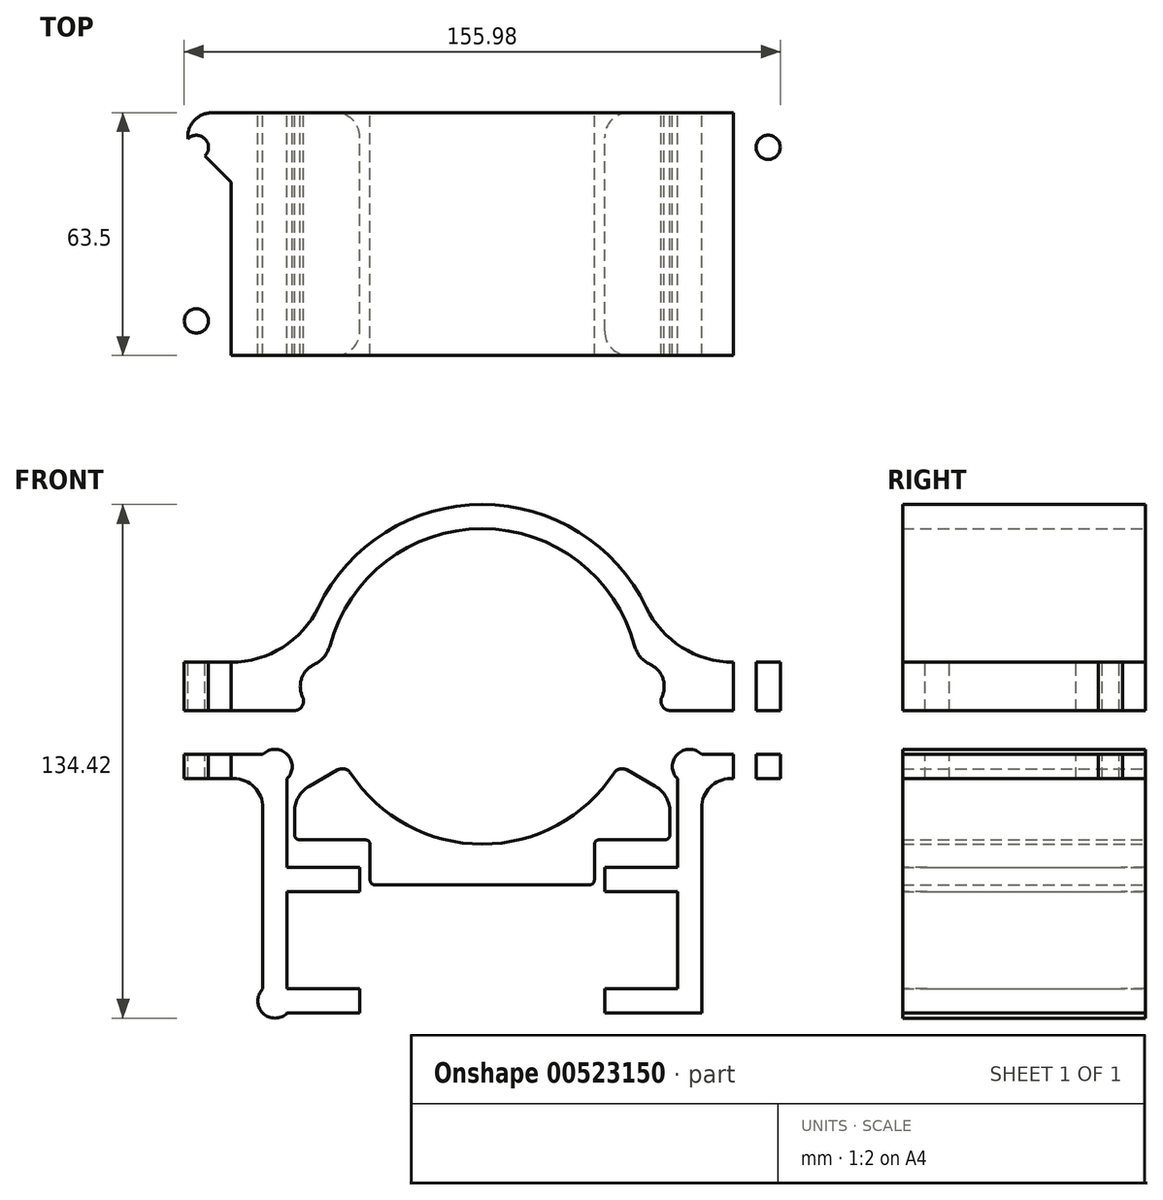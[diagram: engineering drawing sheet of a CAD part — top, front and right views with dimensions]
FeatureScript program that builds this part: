
annotation { "Feature Type Name" : "Feature", "Feature Type Description" : "" }
export const myFeature = defineFeature(function(context is Context, id is Id, definition is map)
    precondition{}
    {
        {
            var Q0;
            Q0=qCreatedBy(makeId("Front.planeOp"),FACE);
            var sketch = newSketch(context, id + "F0", { "sketchPlane" : qUnion([Q0])});
            skArc(sketch, "E0", {"start": v(-40.79, -6.33) * mm, "mid": v(-40.79, -6.34) * mm, "end": v(-40.78, -6.35) * mm});
            skArc(sketch, "E1", {"start": v(-43.98, 5.74) * mm, "mid": v(-47.25, 2.14) * mm, "end": v(-47.01, -2.72) * mm});
            skArc(sketch, "E2", {"start": v(47.01, -2.72) * mm, "mid": v(47.25, 2.14) * mm, "end": v(43.98, 5.74) * mm});
            skArc(sketch, "E3.trimOffspring", {"start": v(39.87, 10.67) * mm, "mid": v(0, 41.28) * mm, "end": v(-39.87, 10.67) * mm});
            skLineSegment(sketch, "E4.bottom", {"start": v(-83.86, 6.35) * mm, "end": v(-65.76, 6.35) * mm});
            skLineSegment(sketch, "E4.top", {"start": v(-83.86, -6.35) * mm, "end": v(-49.3, -6.35) * mm});
            skLineSegment(sketch, "E4.left", {"start": v(-83.86, 6.35) * mm, "end": v(-83.86, -6.35) * mm});
            skLineSegment(sketch, "E4.right", {"start": v(83.86, 6.35) * mm, "end": v(83.86, -6.35) * mm});
            skLineSegment(sketch, "E5.trimOffspring", {"start": v(-41.28, 6.35) * mm, "end": v(-40.78, 6.35) * mm});
            skLineSegment(sketch, "E6.trimOffspring", {"start": v(40.78, 6.35) * mm, "end": v(41.28, 6.35) * mm});
            skLineSegment(sketch, "E7.trimOffspring", {"start": v(49.3, -6.35) * mm, "end": v(83.86, -6.35) * mm});
            skLineSegment(sketch, "E8", {"start": v(-37.88, -21.87) * mm, "end": v(-41.24, -23.81) * mm});
            skLineSegment(sketch, "E9.MirrorCS", {"start": v(37.88, -21.87) * mm, "end": v(41.24, -23.81) * mm});
            skPoint(sketch, "E10.orphan", {"position": v(-49.1, -28.35) * mm});
            skPoint(sketch, "E11.orphan", {"position": v(49.1, -28.35) * mm});
            skArc(sketch, "E12.trimOffspring", {"start": v(40.78, -6.35) * mm, "mid": v(40.79, -6.34) * mm, "end": v(40.79, -6.33) * mm});
            skArc(sketch, "E13.trimOffspring", {"start": v(-34.49, -22.67) * mm, "mid": v(0, -41.28) * mm, "end": v(34.49, -22.67) * mm});
            skLineSegment(sketch, "E14.trimOffspring", {"start": v(65.76, 6.35) * mm, "end": v(83.86, 6.35) * mm});
            skArc(sketch, "E15.trimOffspring", {"start": v(42.89, 20.7) * mm, "mid": v(0, 47.62) * mm, "end": v(-42.89, 20.7) * mm});
            skArc(sketch, "E16.filletArc", {"start": v(-49.3, -6.35) * mm, "mid": v(-47.16, -5.17) * mm, "end": v(-47.01, -2.72) * mm});
            skArc(sketch, "E17.filletArc", {"start": v(47.01, -2.72) * mm, "mid": v(47.16, -5.17) * mm, "end": v(49.3, -6.35) * mm});
            skPoint(sketch, "E18.visualSharp", {"position": v(-47.2, 6.35) * mm});
            skArc(sketch, "E18.filletArc", {"start": v(-65.76, 6.35) * mm, "mid": v(-52.26, 10.24) * mm, "end": v(-42.89, 20.7) * mm});
            skPoint(sketch, "E19.visualSharp", {"position": v(47.2, 6.35) * mm});
            skArc(sketch, "E19.filletArc", {"start": v(42.89, 20.7) * mm, "mid": v(52.26, 10.24) * mm, "end": v(65.76, 6.35) * mm});
            skLineSegment(sketch, "E20", {"start": v(-41.24, -23.81) * mm, "end": v(-45.29, -26.15) * mm});
            skLineSegment(sketch, "E21", {"start": v(-29.34, -51.94) * mm, "end": v(29.34, -51.94) * mm});
            skLineSegment(sketch, "E22", {"start": v(45.29, -26.15) * mm, "end": v(41.24, -23.81) * mm});
            skPoint(sketch, "E23.visualSharp", {"position": v(-40.79, 6.33) * mm});
            skArc(sketch, "E23.filletArc", {"start": v(-43.98, 5.74) * mm, "mid": v(-41.39, 7.75) * mm, "end": v(-39.87, 10.67) * mm});
            skPoint(sketch, "E24.visualSharp", {"position": v(40.79, 6.33) * mm});
            skArc(sketch, "E24.filletArc", {"start": v(39.87, 10.67) * mm, "mid": v(41.39, 7.75) * mm, "end": v(43.98, 5.74) * mm});
            skLineSegment(sketch, "E25", {"start": v(-49.1, -32.75) * mm, "end": v(-49.1, -40.14) * mm});
            skLineSegment(sketch, "E26", {"start": v(49.1, -32.75) * mm, "end": v(49.1, -40.14) * mm});
            skPoint(sketch, "E27.visualSharp", {"position": v(-35.75, -20.64) * mm});
            skArc(sketch, "E27.filletArc", {"start": v(-34.49, -22.67) * mm, "mid": v(-36.03, -21.6) * mm, "end": v(-37.88, -21.87) * mm});
            skPoint(sketch, "E28.visualSharp", {"position": v(35.75, -20.64) * mm});
            skArc(sketch, "E28.filletArc", {"start": v(37.88, -21.87) * mm, "mid": v(36.03, -21.6) * mm, "end": v(34.49, -22.67) * mm});
            skArc(sketch, "E29.filletArc", {"start": v(-45.29, -26.15) * mm, "mid": v(-48.08, -28.94) * mm, "end": v(-49.1, -32.75) * mm});
            skArc(sketch, "E30.filletArc", {"start": v(49.1, -32.75) * mm, "mid": v(48.08, -28.94) * mm, "end": v(45.29, -26.15) * mm});
            skLineSegment(sketch, "E31.bottom", {"start": v(-51.07, -53.74) * mm, "end": v(-32.02, -53.74) * mm});
            skLineSegment(sketch, "E31.top", {"start": v(-51.07, -79.14) * mm, "end": v(-32.02, -79.14) * mm});
            skLineSegment(sketch, "E31.left", {"start": v(-51.07, -53.74) * mm, "end": v(-51.07, -79.14) * mm});
            skLineSegment(sketch, "E31.right", {"start": v(51.07, -53.74) * mm, "end": v(51.07, -79.14) * mm});
            skPoint(sketch, "E31.middle", {"position": v(0, -66.44) * mm});
            skLineSegment(sketch, "E32.0", {"start": v(-51.07, -85.49) * mm, "end": v(-32.02, -85.49) * mm});
            skLineSegment(sketch, "E32.1", {"start": v(-57.42, -47.39) * mm, "end": v(-57.42, -79.14) * mm});
            skLineSegment(sketch, "E32.2", {"start": v(-51.07, -47.39) * mm, "end": v(-32.02, -47.39) * mm});
            skLineSegment(sketch, "E32.3", {"start": v(57.42, -47.39) * mm, "end": v(57.42, -85.49) * mm});
            skLineSegment(sketch, "E33", {"start": v(-32.02, -47.39) * mm, "end": v(-32.02, -53.74) * mm});
            skLineSegment(sketch, "E34.MirrorCS", {"start": v(32.02, -47.39) * mm, "end": v(32.02, -53.74) * mm});
            skLineSegment(sketch, "E35.trimOffspring", {"start": v(32.02, -53.74) * mm, "end": v(51.07, -53.74) * mm});
            skLineSegment(sketch, "E36.trimOffspring", {"start": v(32.02, -47.39) * mm, "end": v(51.07, -47.39) * mm});
            skLineSegment(sketch, "E37.trimOffspring", {"start": v(32.02, -79.14) * mm, "end": v(32.02, -85.49) * mm});
            skLineSegment(sketch, "E38.trimOffspring", {"start": v(-32.02, -79.14) * mm, "end": v(-32.02, -85.49) * mm});
            skLineSegment(sketch, "E39.trimOffspring", {"start": v(32.02, -79.14) * mm, "end": v(51.07, -79.14) * mm});
            skLineSegment(sketch, "E40.trimOffspring", {"start": v(32.02, -85.49) * mm, "end": v(57.42, -85.49) * mm});
            skArc(sketch, "E41", {"start": v(-57.42, -79.14) * mm, "mid": v(-57.42, -85.49) * mm, "end": v(-51.07, -85.49) * mm});
            skPoint(sketch, "E41.third.point", {"position": v(-51.07, -85.49) * mm});
            skLineSegment(sketch, "E42", {"start": v(-51.07, -47.39) * mm, "end": v(-51.07, -24.13) * mm});
            skLineSegment(sketch, "E43", {"start": v(-57.42, -17.78) * mm, "end": v(-83.86, -17.78) * mm});
            skLineSegment(sketch, "E44", {"start": v(-83.86, -17.78) * mm, "end": v(-83.86, -24.13) * mm});
            skLineSegment(sketch, "E45", {"start": v(-83.86, -24.13) * mm, "end": v(-65.04, -24.13) * mm});
            skLineSegment(sketch, "E46", {"start": v(-57.42, -31.75) * mm, "end": v(-57.42, -47.39) * mm});
            skLineSegment(sketch, "E47.top", {"start": v(-49.1, -40.14) * mm, "end": v(-29.34, -40.14) * mm});
            skLineSegment(sketch, "E47.right", {"start": v(-29.34, -51.94) * mm, "end": v(-29.34, -40.14) * mm});
            skLineSegment(sketch, "E48.MirrorCS", {"start": v(29.34, -51.94) * mm, "end": v(29.34, -40.14) * mm});
            skLineSegment(sketch, "E49.MirrorCS", {"start": v(49.1, -40.14) * mm, "end": v(29.34, -40.14) * mm});
            skPoint(sketch, "E50.visualSharp", {"position": v(-57.42, -24.13) * mm});
            skArc(sketch, "E50.filletArc", {"start": v(-57.42, -31.75) * mm, "mid": v(-59.65, -26.37) * mm, "end": v(-65.04, -24.13) * mm});
            skArc(sketch, "E51", {"start": v(-51.07, -24.13) * mm, "mid": v(-51.07, -17.78) * mm, "end": v(-57.42, -17.78) * mm});
            skPoint(sketch, "E51.third.point", {"position": v(-51.07, -24.13) * mm});
            skArc(sketch, "E52.MirrorCS", {"start": v(51.07, -24.13) * mm, "mid": v(51.07, -17.78) * mm, "end": v(57.42, -17.78) * mm});
            skLineSegment(sketch, "E53.MirrorCS", {"start": v(57.42, -17.78) * mm, "end": v(83.86, -17.78) * mm});
            skLineSegment(sketch, "E54.MirrorCS", {"start": v(83.86, -17.78) * mm, "end": v(83.86, -24.13) * mm});
            skLineSegment(sketch, "E55.MirrorCS", {"start": v(83.86, -24.13) * mm, "end": v(65.04, -24.13) * mm});
            skArc(sketch, "E56.MirrorCS", {"start": v(57.42, -31.75) * mm, "mid": v(59.65, -26.37) * mm, "end": v(65.04, -24.13) * mm});
            skLineSegment(sketch, "E57.MirrorCS", {"start": v(57.42, -31.75) * mm, "end": v(57.42, -47.39) * mm});
            skLineSegment(sketch, "E58.MirrorCS", {"start": v(51.07, -47.39) * mm, "end": v(51.07, -24.13) * mm});
            skPoint(sketch, "E59.orphan", {"position": v(51.07, -53.74) * mm});
            skSolve(sketch);
        }
        {
            var Q0;
            Q0=makeQuery(id+"F0.imprint","IMPRINT",FACE,{"disambiguationData":[TD([[makeQuery(id+"F0.imprint","IMPRINT",EDGE,{"derivedFrom":sQuery(id+"F0.wireOp",EDGE,"E1")}),-1.0]])]});
            var Q1;
            Q1=makeQuery(id+"F0.imprint","IMPRINT",FACE,{"disambiguationData":[TD([[makeQuery(id+"F0.imprint","IMPRINT",EDGE,{"derivedFrom":sQuery(id+"F0.wireOp",EDGE,"E31.bottom")}),1.0]])]});
            var Q2;
            Q2=makeQuery(id+"F0.imprint","IMPRINT",FACE,{"disambiguationData":[TD([[makeQuery(id+"F0.imprint","IMPRINT",EDGE,{"derivedFrom":sQuery(id+"F0.wireOp",EDGE,"E8")}),1.0]])]});
            var Q3;
            Q3=makeQuery(id+"F0.imprint","IMPRINT",FACE,{"disambiguationData":[TD([[makeQuery(id+"F0.imprint","IMPRINT",EDGE,{"derivedFrom":sQuery(id+"F0.wireOp",EDGE,"E31.right")}),1.0]])]});
            extrude(context, id + "F1", {"entities" : qUnion([Q0, Q1, Q2, Q3]), "depth" : 63.5 * mm, "offsetDistance" : 25.4 * mm});
        }
        {
            var Q0;
            Q0=makeQuery(id+"F1.opExtrude","SWEPT_FACE",FACE,{"disambiguationData":[OSD([sQuery(id+"F0.wireOp",EDGE,"E14.trimOffspring")])]});
            var sketch = newSketch(context, id + "F2", { "sketchPlane" : qUnion([Q0])});
            skLineSegment(sketch, "E60.0.0", {"start": v(-65.76, 0) * mm, "end": v(-83.86, 0) * mm});
            skLineSegment(sketch, "E60.0.1", {"start": v(-83.86, 0) * mm, "end": v(-83.86, -63.5) * mm});
            skLineSegment(sketch, "E60.0.2", {"start": v(-83.86, -63.5) * mm, "end": v(-65.76, -63.5) * mm});
            skLineSegment(sketch, "E60.0.3", {"start": v(-65.76, -63.5) * mm, "end": v(-65.76, 0) * mm});
            skLineSegment(sketch, "E61", {"start": v(-83.86, 0) * mm, "end": v(-77.06, -6.8) * mm});
            skCircle(sketch, "E62", {"center": v(-74.81, -9.05) * mm, "radius": 3.18 * mm});
            skLineSegment(sketch, "E63.trimOffspring", {"start": v(-72.57, -11.3) * mm, "end": v(-65.76, -18.1) * mm});
            skCircle(sketch, "E64.MirrorC", {"center": v(74.81, -9.05) * mm, "radius": 3.18 * mm});
            skPoint(sketch, "E65", {"position": v(-83.86, -31.75) * mm});
            skLineSegment(sketch, "E66", {"start": v(-83.86, -31.75) * mm, "end": v(-98.03, -31.75) * mm});
            skCircle(sketch, "E67.MirrorC", {"center": v(-74.81, -54.45) * mm, "radius": 3.18 * mm});
            skCircle(sketch, "E68.MirrorC", {"center": v(74.81, -54.45) * mm, "radius": 3.18 * mm});
            skSolve(sketch);
        }
        {
            var Q0;
            {var subQ0=sQuery(id+"F2.wireOp",EDGE,"E62");var subQ1=makeQuery(id+"F2.imprint","INTERSECT",VERTEX,{"derivedFrom":[sQuery(id+"F2.wireOp",EDGE,"E61"),subQ0]});Q0=makeQuery(id+"F2.imprint","IMPRINT",FACE,{"disambiguationData":[TD([[makeQuery(id+"F2.imprint","IMPRINT",EDGE,{"disambiguationData":[TD([[subQ1,-1.0]])],"derivedFrom":subQ0}),1.0]])]});}
            var Q1;
            Q1=makeQuery(id+"F2.imprint","IMPRINT",FACE,{"disambiguationData":[TD([[makeQuery(id+"F2.imprint","IMPRINT",EDGE,{"derivedFrom":sQuery(id+"F2.wireOp",EDGE,"E67.MirrorC")}),-1.0]])]});
            var Q2;
            Q2=makeQuery(id+"F2.imprint","IMPRINT",FACE,{"disambiguationData":[TD([[makeQuery(id+"F2.imprint","IMPRINT",EDGE,{"derivedFrom":sQuery(id+"F2.wireOp",EDGE,"E68.MirrorC")}),1.0]])]});
            var Q3;
            Q3=makeQuery(id+"F2.imprint","IMPRINT",FACE,{"disambiguationData":[TD([[makeQuery(id+"F2.imprint","IMPRINT",EDGE,{"derivedFrom":sQuery(id+"F2.wireOp",EDGE,"E64.MirrorC")}),-1.0]])]});
            extrude(context, id + "F3", {"entities" : qUnion([Q0, Q1, Q2, Q3]), "operationType" : NewBodyOperationType.REMOVE, "endBound" : BoundingType.THROUGH_ALL, "oppositeDirection" : true, "depth" : 76.2 * mm, "offsetDistance" : 25.4 * mm});
        }
        {
            var Q0;
            Q0=makeQuery(id+"F1.opExtrude","CAP_EDGE",EDGE,{"disambiguationData":[OSD([sQuery(id+"F0.wireOp",EDGE,"E4.left")])],"isStart":true});
            var Q1;
            Q1=makeQuery(id+"F1.opExtrude","CAP_EDGE",EDGE,{"disambiguationData":[OSD([sQuery(id+"F0.wireOp",EDGE,"E44")])],"isStart":true});
            var Q2;
            Q2=makeQuery(id+"F1.opExtrude","CAP_EDGE",EDGE,{"disambiguationData":[OSD([sQuery(id+"F0.wireOp",EDGE,"E4.left")])],"isStart":false});
            var Q3;
            Q3=makeQuery(id+"F1.opExtrude","CAP_EDGE",EDGE,{"disambiguationData":[OSD([sQuery(id+"F0.wireOp",EDGE,"E44")])],"isStart":false});
            var Q4;
            Q4=makeQuery(id+"F1.opExtrude","CAP_EDGE",EDGE,{"disambiguationData":[OSD([sQuery(id+"F0.wireOp",EDGE,"E4.right")])],"isStart":false});
            var Q5;
            Q5=makeQuery(id+"F1.opExtrude","CAP_EDGE",EDGE,{"disambiguationData":[OSD([sQuery(id+"F0.wireOp",EDGE,"E4.right")])],"isStart":true});
            var Q6;
            Q6=makeQuery(id+"F1.opExtrude","CAP_EDGE",EDGE,{"disambiguationData":[OSD([sQuery(id+"F0.wireOp",EDGE,"E54.MirrorCS")])],"isStart":true});
            var Q7;
            Q7=makeQuery(id+"F1.opExtrude","CAP_EDGE",EDGE,{"disambiguationData":[OSD([sQuery(id+"F0.wireOp",EDGE,"E54.MirrorCS")])],"isStart":false});
            var Q8;
            Q8=makeQuery(id+"F1.opExtrude","CAP_EDGE",EDGE,{"disambiguationData":[OSD([sQuery(id+"F0.wireOp",EDGE,"E37.trimOffspring")])],"isStart":true});
            var Q9;
            Q9=makeQuery(id+"F1.opExtrude","CAP_EDGE",EDGE,{"disambiguationData":[OSD([sQuery(id+"F0.wireOp",EDGE,"E34.MirrorCS")])],"isStart":true});
            var Q10;
            Q10=makeQuery(id+"F1.opExtrude","CAP_EDGE",EDGE,{"disambiguationData":[OSD([sQuery(id+"F0.wireOp",EDGE,"E33")])],"isStart":true});
            var Q11;
            Q11=makeQuery(id+"F1.opExtrude","CAP_EDGE",EDGE,{"disambiguationData":[OSD([sQuery(id+"F0.wireOp",EDGE,"E38.trimOffspring")])],"isStart":true});
            var Q12;
            Q12=makeQuery(id+"F1.opExtrude","CAP_EDGE",EDGE,{"disambiguationData":[OSD([sQuery(id+"F0.wireOp",EDGE,"E37.trimOffspring")])],"isStart":false});
            var Q13;
            Q13=makeQuery(id+"F1.opExtrude","CAP_EDGE",EDGE,{"disambiguationData":[OSD([sQuery(id+"F0.wireOp",EDGE,"E34.MirrorCS")])],"isStart":false});
            var Q14;
            Q14=makeQuery(id+"F1.opExtrude","CAP_EDGE",EDGE,{"disambiguationData":[OSD([sQuery(id+"F0.wireOp",EDGE,"E33")])],"isStart":false});
            var Q15;
            Q15=makeQuery(id+"F1.opExtrude","CAP_EDGE",EDGE,{"disambiguationData":[OSD([sQuery(id+"F0.wireOp",EDGE,"E38.trimOffspring")])],"isStart":false});
            fillet(context, id + "F4", {"entities" : qUnion([Q0, Q1, Q2, Q3, Q4, Q5, Q6, Q7, Q8, Q9, Q10, Q11, Q12, Q13, Q14, Q15]), "radius" : 6.35 * mm, "tangentPropagation" : true, "allowEdgeOverflow" : false});
        }
        {
            var Q0;
            Q0=makeQuery(id+"F1.opExtrude","SWEPT_EDGE",EDGE,{"disambiguationData":[OSD([sQuery(id+"F0.wireOp",EDGE,"E48.MirrorCS"),sQuery(id+"F0.wireOp",EDGE,"E49.MirrorCS")])]});
            var Q1;
            Q1=makeQuery(id+"F1.opExtrude","SWEPT_EDGE",EDGE,{"disambiguationData":[OSD([sQuery(id+"F0.wireOp",EDGE,"E21"),sQuery(id+"F0.wireOp",EDGE,"E48.MirrorCS")])]});
            var Q2;
            Q2=makeQuery(id+"F1.opExtrude","SWEPT_EDGE",EDGE,{"disambiguationData":[OSD([sQuery(id+"F0.wireOp",EDGE,"E21"),sQuery(id+"F0.wireOp",EDGE,"E47.right")])]});
            var Q3;
            Q3=makeQuery(id+"F1.opExtrude","SWEPT_EDGE",EDGE,{"disambiguationData":[OSD([sQuery(id+"F0.wireOp",EDGE,"E47.top"),sQuery(id+"F0.wireOp",EDGE,"E47.right")])]});
            var Q4;
            Q4=makeQuery(id+"F1.opExtrude","SWEPT_EDGE",EDGE,{"disambiguationData":[OSD([sQuery(id+"F0.wireOp",EDGE,"E26"),sQuery(id+"F0.wireOp",EDGE,"E49.MirrorCS")])]});
            var Q5;
            Q5=makeQuery(id+"F1.opExtrude","SWEPT_EDGE",EDGE,{"disambiguationData":[OSD([sQuery(id+"F0.wireOp",EDGE,"E25"),sQuery(id+"F0.wireOp",EDGE,"E47.top")])]});
            fillet(context, id + "F5", {"entities" : qUnion([Q0, Q1, Q2, Q3, Q4, Q5]), "radius" : 1.27 * mm, "tangentPropagation" : true, "allowEdgeOverflow" : false});
        }
    });
